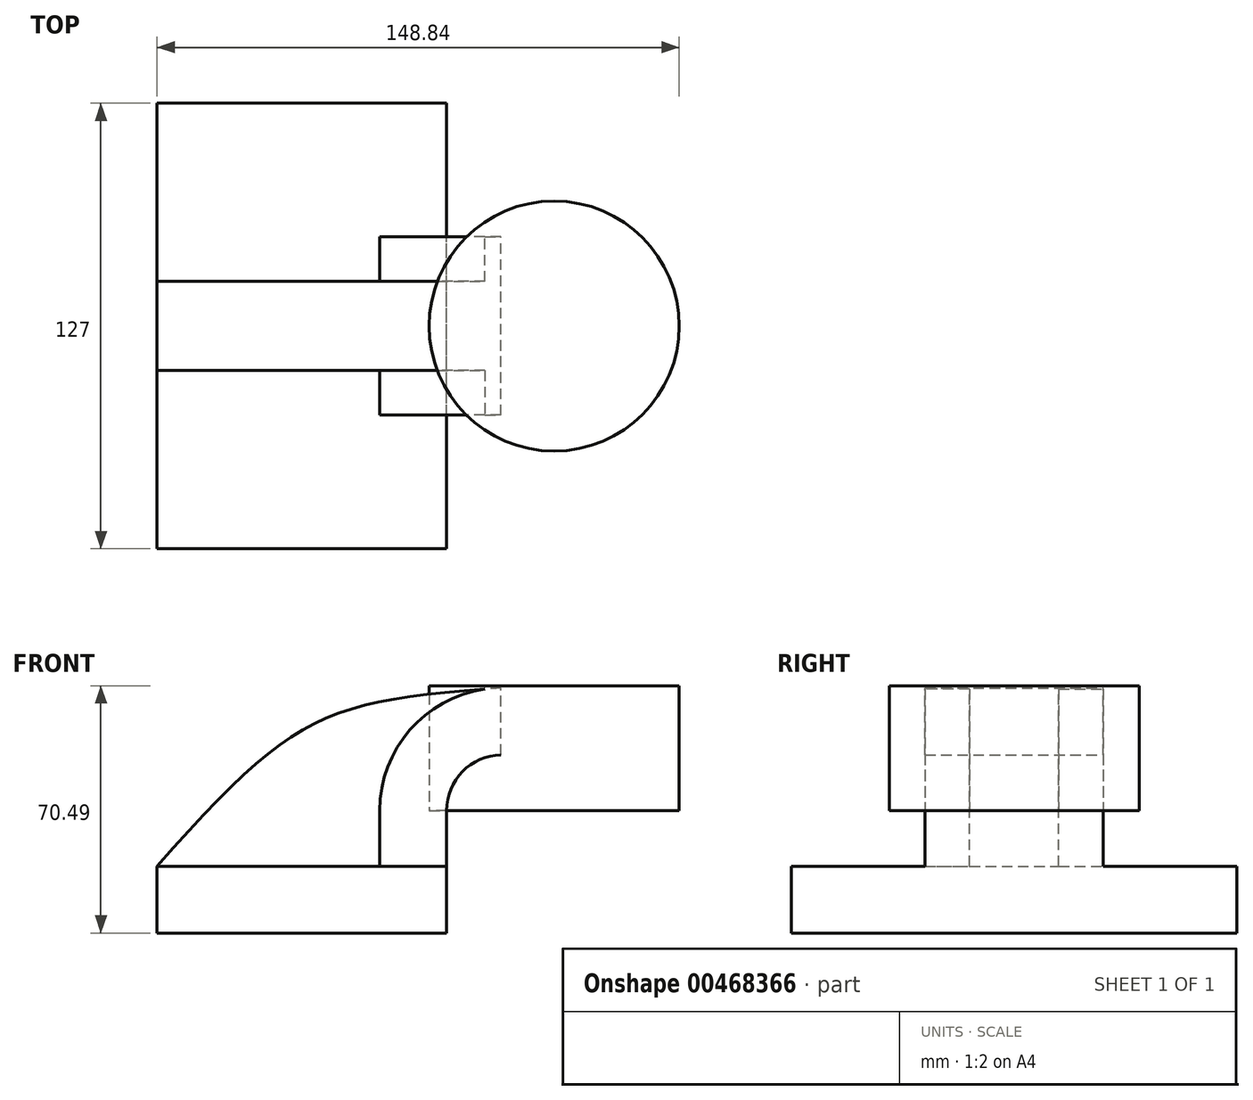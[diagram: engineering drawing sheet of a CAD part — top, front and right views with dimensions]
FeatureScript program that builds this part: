
annotation { "Feature Type Name" : "Feature", "Feature Type Description" : "" }
export const myFeature = defineFeature(function(context is Context, id is Id, definition is map)
    precondition{}
    {
        {
            var Q0;
            Q0=qCreatedBy(makeId("Front.planeOp"),FACE);
            var sketch = newSketch(context, id + "F0", { "sketchPlane" : qUnion([Q0])});
            skLineSegment(sketch, "E0.bottom", {"start": v(41.27, 9.53) * mm, "end": v(-41.28, 9.53) * mm});
            skLineSegment(sketch, "E0.top", {"start": v(41.28, -9.52) * mm, "end": v(-41.27, -9.52) * mm});
            skLineSegment(sketch, "E0.left", {"start": v(41.28, 9.53) * mm, "end": v(41.28, -9.52) * mm});
            skLineSegment(sketch, "E0.right", {"start": v(-41.28, 9.53) * mm, "end": v(-41.27, -9.52) * mm});
            skPoint(sketch, "E0.middle", {"position": v(0, 0) * mm});
            skLineSegment(sketch, "E1.bottom", {"start": v(56.76, 25.4) * mm, "end": v(107.56, 25.4) * mm});
            skLineSegment(sketch, "E1.top", {"start": v(56.76, 60.96) * mm, "end": v(107.56, 60.96) * mm});
            skLineSegment(sketch, "E1.left", {"start": v(56.76, 25.4) * mm, "end": v(56.76, 60.96) * mm});
            skLineSegment(sketch, "E1.right", {"start": v(107.56, 25.4) * mm, "end": v(107.56, 60.96) * mm});
            skPoint(sketch, "E1.middle", {"position": v(82.16, 43.18) * mm});
            skLineSegment(sketch, "E2", {"start": v(41.27, 9.53) * mm, "end": v(41.27, 25.4) * mm});
            skArc(sketch, "E3", {"start": v(41.27, 25.4) * mm, "mid": v(45.92, 36.63) * mm, "end": v(57.15, 41.28) * mm});
            skLineSegment(sketch, "E4", {"start": v(57.15, 41.28) * mm, "end": v(71.92, 41.28) * mm});
            skLineSegment(sketch, "E5.0", {"start": v(57.15, 60.33) * mm, "end": v(71.92, 60.33) * mm});
            skArc(sketch, "E5.1", {"start": v(22.23, 25.4) * mm, "mid": v(32.45, 50.1) * mm, "end": v(57.15, 60.33) * mm});
            skLineSegment(sketch, "E5.2", {"start": v(22.22, 9.53) * mm, "end": v(22.22, 25.4) * mm});
            skFitSpline(sketch, "E6", {"points": [v(-41.28, 9.52) * mm, v(57.15, 60.33) * mm], "startDerivative": vector(115.9, 130.7) * mm, "endDerivative": vector(153.85, 10.64) * mm});
            skLineSegment(sketch, "E7", {"start": v(71.92, 25.4) * mm, "end": v(71.92, 60.96) * mm});
            skSolve(sketch);
        }
        {
            var Q0;
            Q0=makeQuery(id+"F0.imprint","IMPRINT",FACE,{"disambiguationData":[TD([[makeQuery(id+"F0.imprint","IMPRINT",EDGE,{"derivedFrom":sQuery(id+"F0.wireOp",EDGE,"E0.top")}),-1.0]])]});
            extrude(context, id + "F1", {"entities" : qUnion([Q0]), "endBound" : BoundingType.SYMMETRIC, "depth" : 127 * mm});
        }
        {
            var Q0;
            {var subQ0=sQuery(id+"F0.wireOp",EDGE,"E2");Q0=makeQuery(id+"F0.imprint","IMPRINT",FACE,{"disambiguationData":[TD([[makeQuery(id+"F0.imprint","IMPRINT",EDGE,{"derivedFrom":subQ0}),1.0]])]});}
            extrude(context, id + "F2", {"entities" : qUnion([Q0]), "operationType" : NewBodyOperationType.ADD, "endBound" : BoundingType.SYMMETRIC, "depth" : 50.8 * mm});
        }
        {
            var Q0;
            {var subQ3=sQuery(id+"F0.wireOp",EDGE,"E5.2");Q0=makeQuery(id+"F0.imprint","IMPRINT",FACE,{"disambiguationData":[TD([[makeQuery(id+"F0.imprint","IMPRINT",EDGE,{"derivedFrom":subQ3}),1.0]])]});}
            extrude(context, id + "F3", {"entities" : qUnion([Q0]), "operationType" : NewBodyOperationType.ADD, "endBound" : BoundingType.SYMMETRIC, "depth" : 25.4 * mm});
        }
        {
            var Q0;
            {var subQ0=sQuery(id+"F0.wireOp",EDGE,"E1.right");Q0=makeQuery(id+"F0.imprint","IMPRINT",FACE,{"disambiguationData":[TD([[makeQuery(id+"F0.imprint","IMPRINT",EDGE,{"derivedFrom":subQ0}),1.0]])]});}
            var Q1;
            Q1=sQuery(id+"F0.wireOp",EDGE,"E7");
            revolve(context, id + "F4", {"entities" : qUnion([Q0]), "axis" : qUnion([Q1]), "revolveType" : RevolveType.FULL});
        }
    });
